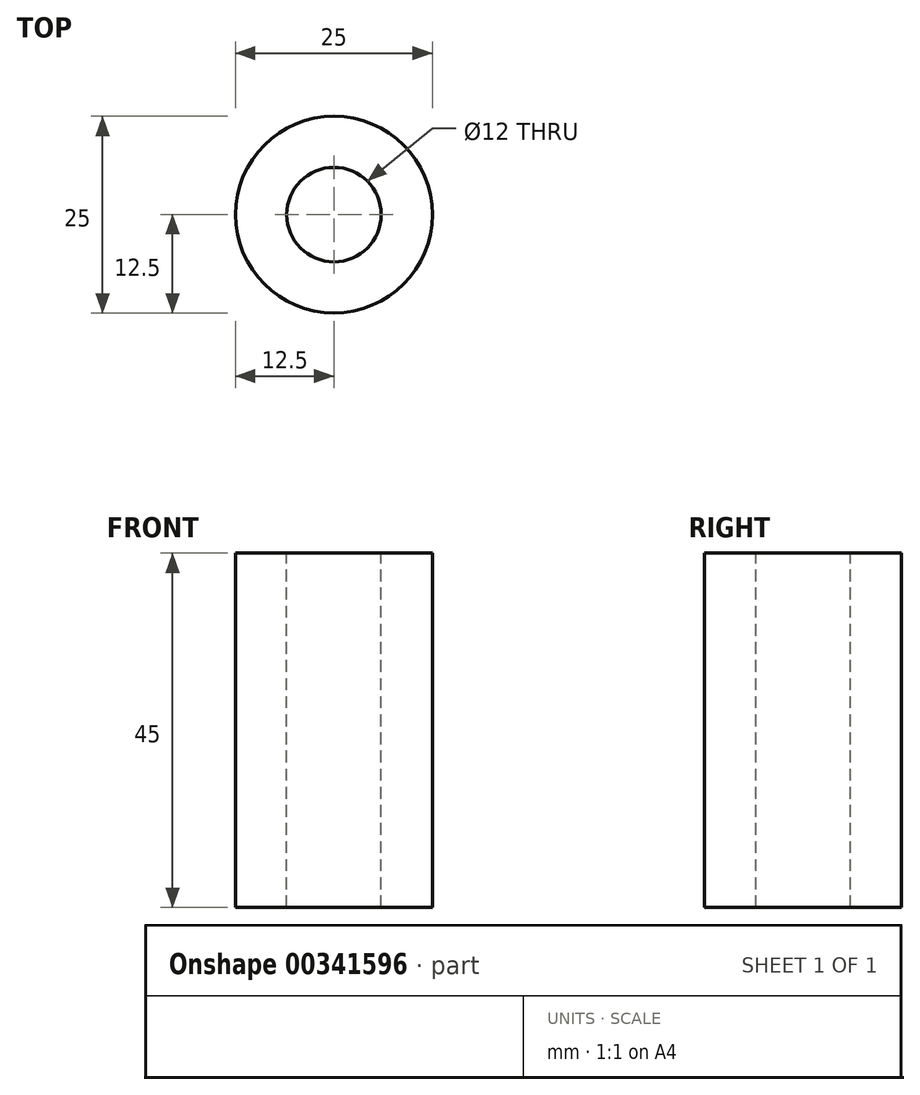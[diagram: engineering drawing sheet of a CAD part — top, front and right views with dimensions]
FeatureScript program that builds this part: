
annotation { "Feature Type Name" : "Feature", "Feature Type Description" : "" }
export const myFeature = defineFeature(function(context is Context, id is Id, definition is map)
    precondition{}
    {
        {
            var Q0;
            Q0=qCreatedBy(makeId("Top.planeOp"),FACE);
            var sketch = newSketch(context, id + "F0", { "sketchPlane" : qUnion([Q0])});
            skCircle(sketch, "E0", {"center": v(0, 0) * mm, "radius": 12.5 * mm});
            skCircle(sketch, "E1", {"center": v(0, 0) * mm, "radius": 6 * mm});
            skSolve(sketch);
        }
        {
            var Q0;
            Q0=makeQuery(id+"F0.imprint","IMPRINT",FACE,{"disambiguationData":[TD([[makeQuery(id+"F0.imprint","IMPRINT",EDGE,{"derivedFrom":sQuery(id+"F0.wireOp",EDGE,"E0")}),1.0]])]});
            extrude(context, id + "F1", {"entities" : qUnion([Q0]), "oppositeDirection" : true, "depth" : 45 * mm});
        }
    });
